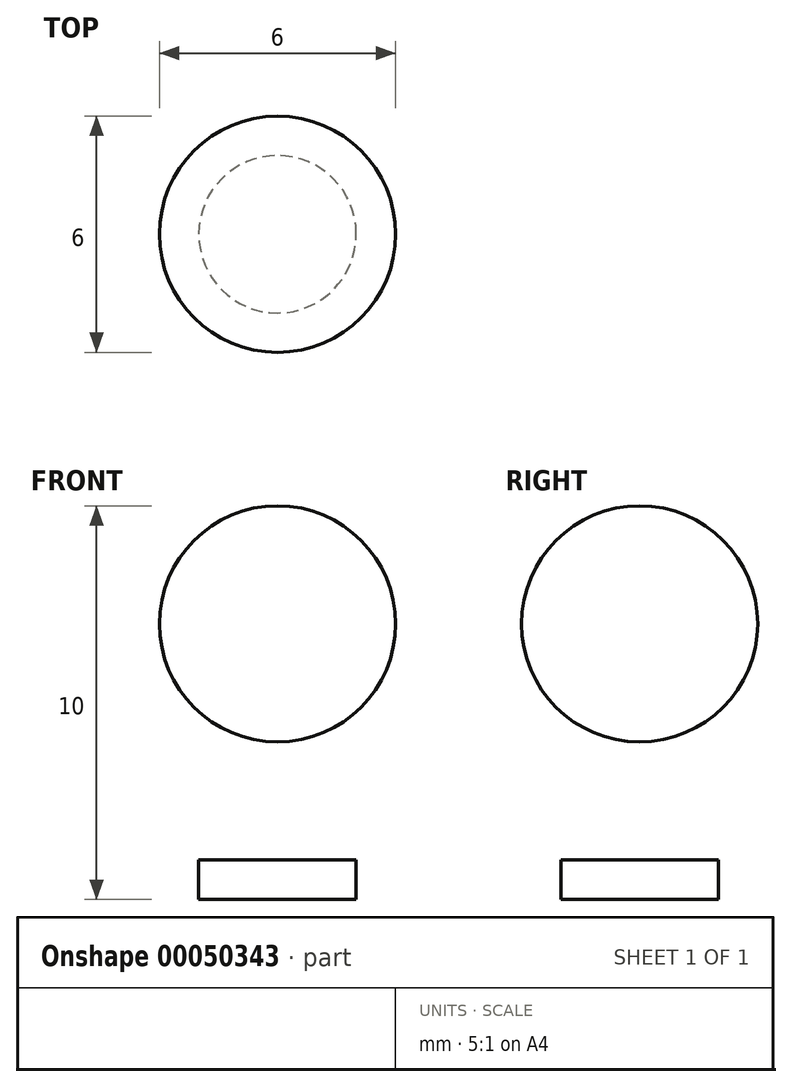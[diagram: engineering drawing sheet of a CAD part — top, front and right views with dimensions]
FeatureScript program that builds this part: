
annotation { "Feature Type Name" : "Feature", "Feature Type Description" : "" }
export const myFeature = defineFeature(function(context is Context, id is Id, definition is map)
    precondition{}
    {
        {
            var Q0;
            Q0=qCreatedBy(makeId("Front.planeOp"),FACE);
            var sketch = newSketch(context, id + "F0", { "sketchPlane" : qUnion([Q0])});
            skArc(sketch, "E0", {"start": v(0, 4) * mm, "mid": v(3, 7) * mm, "end": v(0, 10) * mm});
            skLineSegment(sketch, "E1.bottom", {"start": v(0, 0) * mm, "end": v(2, 0) * mm});
            skLineSegment(sketch, "E1.top", {"start": v(0, 1) * mm, "end": v(2, 1) * mm});
            skLineSegment(sketch, "E1.left", {"start": v(0, 0) * mm, "end": v(0, 1) * mm});
            skLineSegment(sketch, "E1.right", {"start": v(2, 0) * mm, "end": v(2, 1) * mm});
            skLineSegment(sketch, "E2", {"start": v(0, 10) * mm, "end": v(0, 4) * mm});
            skSolve(sketch);
        }
        {
            var Q0;
            Q0=makeQuery(id+"F0.imprint","IMPRINT",FACE,{"disambiguationData":[TD([[makeQuery(id+"F0.imprint","IMPRINT",EDGE,{"derivedFrom":sQuery(id+"F0.wireOp",EDGE,"E0")}),1.0]])]});
            var Q1;
            Q1=makeQuery(id+"F0.imprint","IMPRINT",FACE,{"disambiguationData":[TD([[makeQuery(id+"F0.imprint","IMPRINT",EDGE,{"derivedFrom":sQuery(id+"F0.wireOp",EDGE,"E1.bottom")}),1.0]])]});
            var Q2;
            Q2=sQuery(id+"F0.wireOp",EDGE,"E2");
            revolve(context, id + "F1", {"entities" : qUnion([Q0, Q1]), "axis" : qUnion([Q2]), "revolveType" : RevolveType.FULL});
        }
    });
